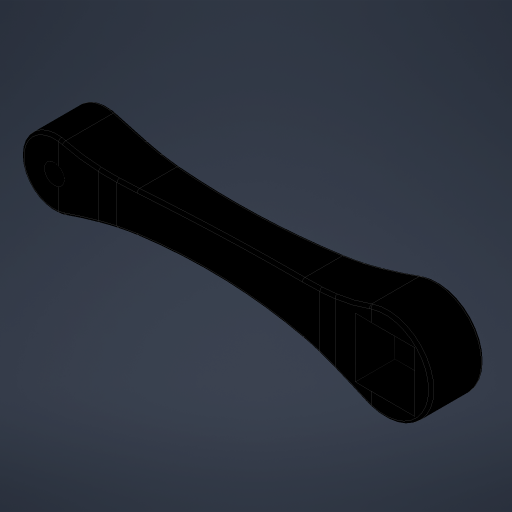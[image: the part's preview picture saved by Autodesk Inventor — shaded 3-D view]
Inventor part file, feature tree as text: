
AUTODESK INVENTOR PART (.ipt)
format: ipt  version: 2023 (Build 270158000, 158)  size: 465,920 bytes
history: native  units: mm
features: extrude x6, sketch x6, fillet x5, chamfer x4
ambient origin geometry x8: Origin, YZ Plane, XZ Plane, XY Plane, X Axis, Y Axis, Z Axis, Center Point
bodies: Solid1 (feature_tree)
feature tree (21):
  extrude  "Extrusion1"  Depth=250.0mm
  extrude  "Extrusion2"  TaperAngle=45.0deg  [1 undecoded]
  extrude  "Extrusion3"  Depth=40.0mm TaperAngle=0.0deg
  chamfer  "Chamfer1"  Distance=10.0mm
  chamfer  "Chamfer2"  Distance=10.0mm
  chamfer  "Chamfer3"  Distance=10.0mm Angle=45.0deg
  chamfer  "Chamfer4"  Distance=10.0mm Angle=45.0deg
  fillet  "Fillet1"  Radius=800.0mm
  extrude  "Extrusion4"  Depth=15.0mm
  fillet  "Fillet2"  Radius=40.0mm
  fillet  "Fillet3"  Radius=300.0mm
  extrude  "Extrusion5"  Depth=200.0mm
  extrude  "Extrusion7"  Depth=22.5mm
  fillet  "Fillet5"  Radius=22.5mm
  fillet  "Fillet6"  Radius=45.0mm
  sketch  "Sketch1"  dims[d0=50.0mm d1=250.0mm]
  sketch  "Sketch2"  dims[d2=70.0mm d3=45.0deg]
  sketch  "Sketch3"  dims[d4=135.0deg d5=40.0mm d6=0.0mm d7=10.0mm d8=0.0mm]
  sketch  "Sketch4"  dims[d9=49.497mm d10=10.0mm d11=0.0mm d12=10.0mm d13=103.787mm d14=45.0deg d15=10.0mm d16=103.786mm d17=45.0deg]
  sketch  "Sketch5"  dims[d18=10.0mm d19=103.786mm d20=45.0deg]
  sketch  "Sketch7"  dims[d21=10.0mm d22=103.787mm d23=45.0deg d24=800.0mm d25=15.0mm d26=40.0mm d27=0.0mm d28=300.0mm d29=200.0mm d30=22.5mm d31=22.5mm d32=45.0mm d33=45.0mm d34=30.0mm d35=0.0mm d40=50.0mm d41=5.0mm d42=0.0mm d43=2.0mm d44=2.0mm]
note: 1 required parameter value undecoded (feature->parameter linkage not recoverable at this tier; creation-order binding heuristic only, values carry confidence <= 0.55)
